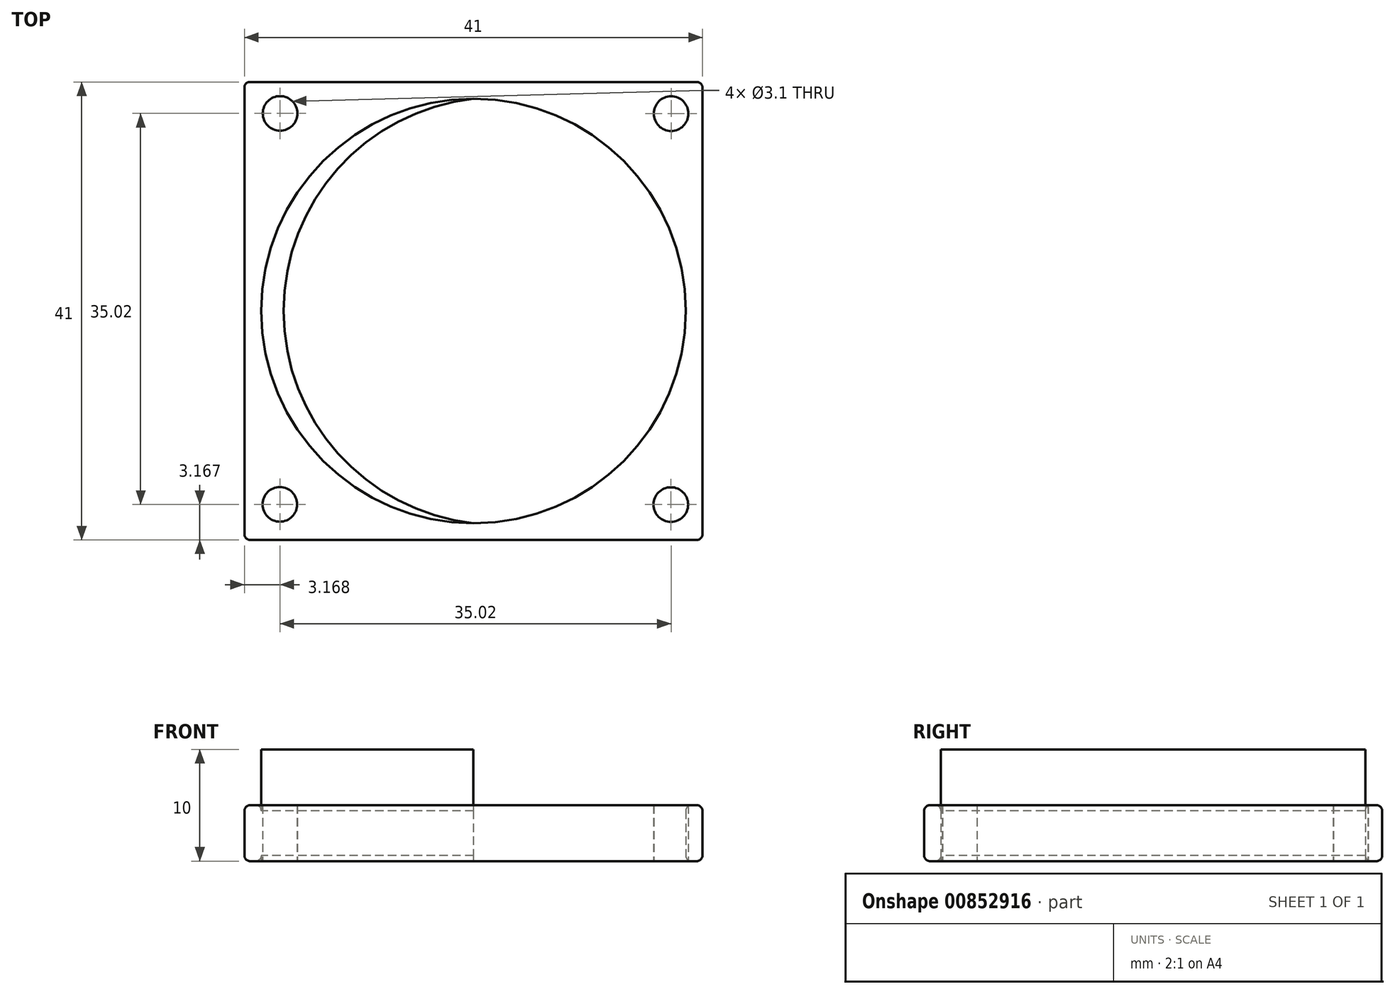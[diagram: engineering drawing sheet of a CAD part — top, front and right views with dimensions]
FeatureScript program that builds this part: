
annotation { "Feature Type Name" : "Feature", "Feature Type Description" : "" }
export const myFeature = defineFeature(function(context is Context, id is Id, definition is map)
    precondition{}
    {
        {
            var Q0;
            Q0=qCreatedBy(makeId("Top.planeOp"),FACE);
            var sketch = newSketch(context, id + "F0", { "sketchPlane" : qUnion([Q0])});
            skCircle(sketch, "E0", {"center": v(0, 0) * mm, "radius": 19 * mm});
            skCircle(sketch, "E1", {"center": v(17.69, 17.67) * mm, "radius": 1.55 * mm});
            skCircle(sketch, "E2.1.0", {"center": v(-17.31, 17.69) * mm, "radius": 1.55 * mm});
            skCircle(sketch, "E2.2.0", {"center": v(-17.33, -17.31) * mm, "radius": 1.55 * mm});
            skCircle(sketch, "E2.3.0", {"center": v(17.67, -17.33) * mm, "radius": 1.55 * mm});
            skPoint(sketch, "E2.center", {"position": v(0.18, 0.18) * mm});
            skLineSegment(sketch, "E3.bottom", {"start": v(-20.5, 20.5) * mm, "end": v(20.5, 20.5) * mm});
            skLineSegment(sketch, "E3.top", {"start": v(-20.5, -20.5) * mm, "end": v(20.5, -20.5) * mm});
            skLineSegment(sketch, "E3.left", {"start": v(-20.5, 20.5) * mm, "end": v(-20.5, -20.5) * mm});
            skLineSegment(sketch, "E3.right", {"start": v(20.5, 20.5) * mm, "end": v(20.5, -20.5) * mm});
            skSolve(sketch);
        }
        {
            var Q0;
            Q0 = qSketchRegion(id + "F0", true);
            extrude(context, id + "F1", {"entities" : qUnion([Q0]), "depth" : 5 * mm, "offsetDistance" : 25 * mm});
        }
        {
            var Q0;
            Q0=makeQuery(id+"F1.opExtrude","SWEPT_FACE",FACE,{"disambiguationData":[OSD([sQuery(id+"F0.wireOp",EDGE,"E3.top")])]});
            var Q1;
            Q1=makeQuery(id+"F1.opExtrude","CAP_EDGE",EDGE,{"disambiguationData":[OSD([sQuery(id+"F0.wireOp",EDGE,"E3.top")])],"isStart":false});
            var Q2;
            Q2=makeQuery(id+"F1.opExtrude","CAP_EDGE",EDGE,{"disambiguationData":[OSD([sQuery(id+"F0.wireOp",EDGE,"E3.right")])],"isStart":false});
            var Q3;
            Q3=makeQuery(id+"F1.opExtrude","CAP_EDGE",EDGE,{"disambiguationData":[OSD([sQuery(id+"F0.wireOp",EDGE,"E3.bottom")])],"isStart":false});
            var Q4;
            Q4=makeQuery(id+"F1.opExtrude","CAP_EDGE",EDGE,{"disambiguationData":[OSD([sQuery(id+"F0.wireOp",EDGE,"E3.bottom")])],"isStart":true});
            var Q5;
            Q5=makeQuery(id+"F1.opExtrude","SWEPT_EDGE",EDGE,{"disambiguationData":[OSD([sQuery(id+"F0.wireOp",EDGE,"E3.bottom"),sQuery(id+"F0.wireOp",EDGE,"E3.left")])]});
            var Q6;
            Q6=makeQuery(id+"F1.opExtrude","CAP_EDGE",EDGE,{"disambiguationData":[OSD([sQuery(id+"F0.wireOp",EDGE,"E3.left")])],"isStart":true});
            var Q7;
            Q7=makeQuery(id+"F1.opExtrude","CAP_EDGE",EDGE,{"disambiguationData":[OSD([sQuery(id+"F0.wireOp",EDGE,"E3.left")])],"isStart":false});
            var Q8;
            Q8=makeQuery(id+"F1.opExtrude","CAP_EDGE",EDGE,{"disambiguationData":[OSD([sQuery(id+"F0.wireOp",EDGE,"E3.right")])],"isStart":true});
            var Q9;
            Q9=makeQuery(id+"F1.opExtrude","CAP_EDGE",EDGE,{"disambiguationData":[OSD([sQuery(id+"F0.wireOp",EDGE,"E0")])],"isStart":true});
            var Q10;
            Q10=makeQuery(id+"F1.opExtrude","CAP_EDGE",EDGE,{"disambiguationData":[OSD([sQuery(id+"F0.wireOp",EDGE,"E0")])],"isStart":false});
            var Q11;
            Q11=makeQuery(id+"F1.opExtrude","SWEPT_EDGE",EDGE,{"disambiguationData":[OSD([sQuery(id+"F0.wireOp",EDGE,"E3.bottom"),sQuery(id+"F0.wireOp",EDGE,"E3.right")])]});
            fillet(context, id + "F2", {"entities" : qUnion([Q0, Q1, Q2, Q3, Q4, Q5, Q6, Q7, Q8, Q9, Q10, Q11]), "radius" : 0.5 * mm, "tangentPropagation" : true, "allowEdgeOverflow" : false});
        }
        {
            var Q0;
            Q0=qCreatedBy(makeId("Top.planeOp"),FACE);
            var sketch = newSketch(context, id + "F3", { "sketchPlane" : qUnion([Q0])});
            skArc(sketch, "E4", {"start": v(0, 19) * mm, "mid": v(-19, 0) * mm, "end": v(0, -19) * mm});
            skArc(sketch, "E5", {"start": v(0, 19) * mm, "mid": v(-17, 0) * mm, "end": v(0, -19) * mm});
            skSolve(sketch);
        }
        {
            var Q0;
            Q0 = qSketchRegion(id + "F3", true);
            extrude(context, id + "F4", {"entities" : qUnion([Q0]), "operationType" : NewBodyOperationType.ADD, "depth" : 10 * mm, "offsetDistance" : 25 * mm});
        }
    });
